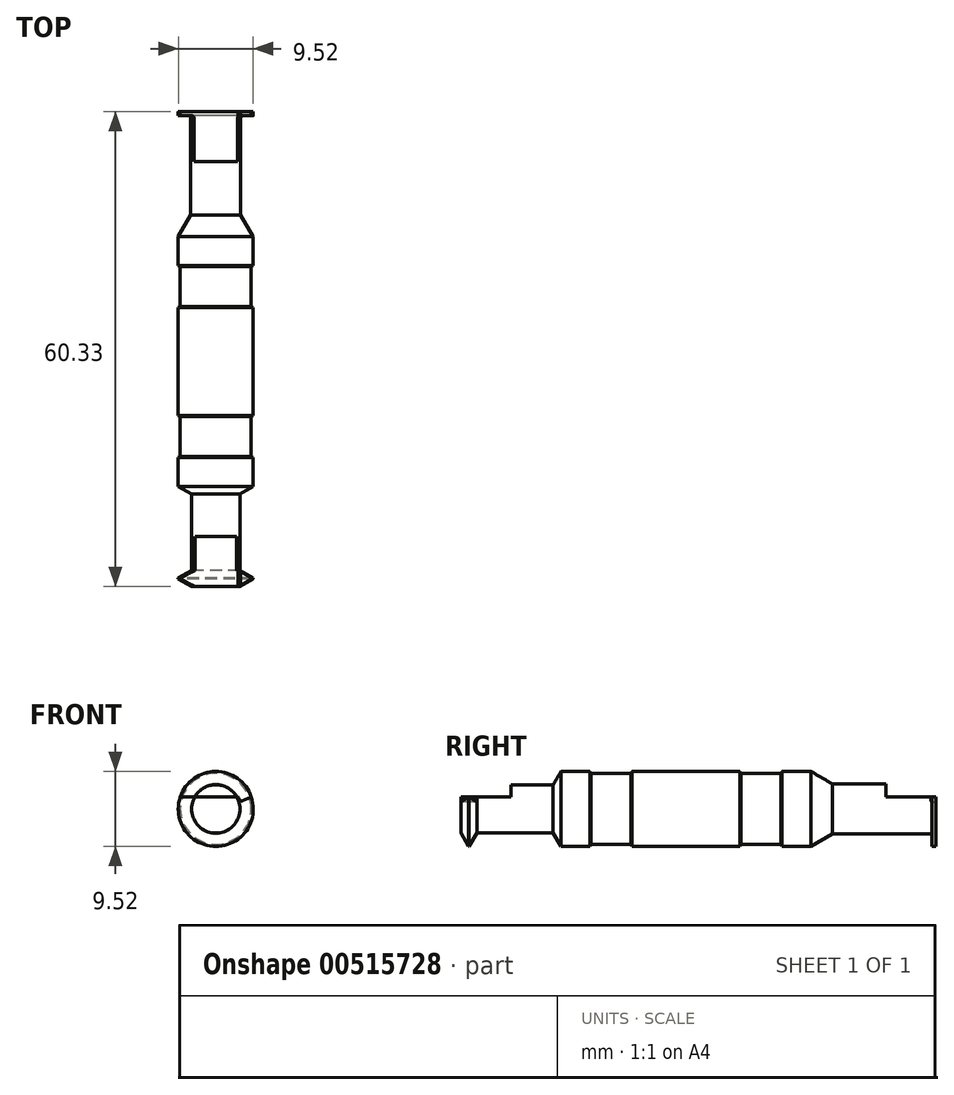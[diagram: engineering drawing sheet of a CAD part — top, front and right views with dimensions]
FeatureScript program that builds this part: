
annotation { "Feature Type Name" : "Feature", "Feature Type Description" : "" }
export const myFeature = defineFeature(function(context is Context, id is Id, definition is map)
    precondition{}
    {
        {
            var Q0;
            Q0=qCreatedBy(makeId("Top.planeOp"),FACE);
            cPlane(context, id + "F0", {"entities" : qUnion([Q0]), "cplaneType" : CPlaneType.OFFSET, "offset" : 1.52 * mm, "width" : 152.4 * mm, "height" : 152.4 * mm});
        }
        {
            var Q0;
            Q0=qCreatedBy(makeId("Right.planeOp"),FACE);
            var sketch = newSketch(context, id + "F1", { "sketchPlane" : qUnion([Q0])});
            skLineSegment(sketch, "E0", {"start": v(0, 4.76) * mm, "end": v(3.66, 4.76) * mm});
            skLineSegment(sketch, "E1", {"start": v(47.62, 4.76) * mm, "end": v(47.62, 0) * mm});
            skLineSegment(sketch, "E2", {"start": v(47.62, 0) * mm, "end": v(-12.7, 0) * mm});
            skLineSegment(sketch, "E3", {"start": v(-12.7, 0) * mm, "end": v(-12.7, 3.07) * mm});
            skLineSegment(sketch, "E4", {"start": v(-12.7, 3.07) * mm, "end": v(-11.72, 4.76) * mm});
            skLineSegment(sketch, "E5", {"start": v(-11.65, 4.76) * mm, "end": v(-10.67, 3.07) * mm});
            skLineSegment(sketch, "E6", {"start": v(-10.67, 3.07) * mm, "end": v(-0.98, 3.07) * mm});
            skLineSegment(sketch, "E7", {"start": v(-0.98, 3.07) * mm, "end": v(0, 4.76) * mm});
            skLineSegment(sketch, "E8", {"start": v(-11.72, 4.76) * mm, "end": v(-11.65, 4.76) * mm});
            skLineSegment(sketch, "E9", {"start": v(47.12, 4.76) * mm, "end": v(47.12, 3.43) * mm});
            skLineSegment(sketch, "E10", {"start": v(46.86, 3.18) * mm, "end": v(34.5, 3.18) * mm});
            skLineSegment(sketch, "E11", {"start": v(34.5, 3.18) * mm, "end": v(31.75, 4.76) * mm});
            skLineSegment(sketch, "E12.trimOffspring", {"start": v(47.12, 4.76) * mm, "end": v(47.62, 4.76) * mm});
            skPoint(sketch, "E13.visualSharp", {"position": v(47.12, 3.18) * mm});
            skArc(sketch, "E13.filletArc", {"start": v(46.86, 3.18) * mm, "mid": v(47.04, 3.25) * mm, "end": v(47.12, 3.43) * mm});
            skLineSegment(sketch, "E14", {"start": v(-11.72, 4.76) * mm, "end": v(-11.68, 4.83) * mm, "construction": true});
            skLineSegment(sketch, "E15", {"start": v(-11.68, 4.83) * mm, "end": v(-11.65, 4.76) * mm, "construction": true});
            skLineSegment(sketch, "E16", {"start": v(3.66, 4.76) * mm, "end": v(3.8, 4.5) * mm});
            skLineSegment(sketch, "E17", {"start": v(3.8, 4.5) * mm, "end": v(8.89, 4.5) * mm});
            skLineSegment(sketch, "E18", {"start": v(8.89, 4.5) * mm, "end": v(9.04, 4.76) * mm});
            skLineSegment(sketch, "E19.trimOffspring", {"start": v(9.04, 4.76) * mm, "end": v(22.71, 4.76) * mm});
            skLineSegment(sketch, "E20", {"start": v(6.35, 4.5) * mm, "end": v(6.35, 0) * mm, "construction": true});
            skLineSegment(sketch, "E21", {"start": v(22.71, 4.76) * mm, "end": v(22.86, 4.5) * mm});
            skLineSegment(sketch, "E22", {"start": v(22.86, 4.5) * mm, "end": v(27.94, 4.5) * mm});
            skLineSegment(sketch, "E23", {"start": v(27.94, 4.5) * mm, "end": v(28.09, 4.76) * mm});
            skLineSegment(sketch, "E24.trimOffspring", {"start": v(28.09, 4.76) * mm, "end": v(31.75, 4.76) * mm});
            skLineSegment(sketch, "E25", {"start": v(25.4, 4.5) * mm, "end": v(25.4, 0) * mm, "construction": true});
            skLineSegment(sketch, "E26", {"start": v(0, 0) * mm, "end": v(-33.3, 0) * mm, "construction": true});
            skSolve(sketch);
        }
        {
            var Q0;
            Q0 = qSketchRegion(id + "F1", true);
            var Q1;
            Q1=sQuery(id+"F1.wireOp",EDGE,"E2");
            revolve(context, id + "F2", {"entities" : qUnion([Q0]), "axis" : qUnion([Q1]), "revolveType" : RevolveType.FULL});
        }
        {
            var Q0;
            Q0=qCreatedBy(id+"F0.planeOp",FACE);
            var sketch = newSketch(context, id + "F3", { "sketchPlane" : qUnion([Q0])});
            skLineSegment(sketch, "E27.bottom", {"start": v(-6.35, -12.7) * mm, "end": v(6.35, -12.7) * mm});
            skLineSegment(sketch, "E27.top", {"start": v(-6.35, -6.35) * mm, "end": v(6.35, -6.35) * mm});
            skLineSegment(sketch, "E27.left", {"start": v(-6.35, -12.7) * mm, "end": v(-6.35, -6.35) * mm});
            skLineSegment(sketch, "E27.right", {"start": v(6.35, -12.7) * mm, "end": v(6.35, -6.35) * mm});
            skLineSegment(sketch, "E28", {"start": v(0, -6.35) * mm, "end": v(0, 0) * mm, "construction": true});
            skLineSegment(sketch, "E29.bottom", {"start": v(-6.35, 41.27) * mm, "end": v(6.35, 41.27) * mm});
            skLineSegment(sketch, "E29.top", {"start": v(-6.35, 47.62) * mm, "end": v(6.35, 47.62) * mm});
            skLineSegment(sketch, "E29.left", {"start": v(-6.35, 41.27) * mm, "end": v(-6.35, 47.62) * mm});
            skLineSegment(sketch, "E29.right", {"start": v(6.35, 41.27) * mm, "end": v(6.35, 47.62) * mm});
            skLineSegment(sketch, "E30", {"start": v(0, 41.27) * mm, "end": v(0, 0) * mm, "construction": true});
            skSolve(sketch);
        }
        {
            var Q0;
            Q0 = qSketchRegion(id + "F3", true);
            extrude(context, id + "F4", {"entities" : qUnion([Q0]), "operationType" : NewBodyOperationType.REMOVE, "endBound" : BoundingType.THROUGH_ALL, "depth" : 25.4 * mm, "offsetDistance" : 25.4 * mm});
        }
        {
            var Q0;
            Q0=makeQuery(id+"F2.opRevolve","SWEPT_FACE",FACE,{"disambiguationData":[OSD([sQuery(id+"F1.wireOp",EDGE,"E3")])]});
            var sketch = newSketch(context, id + "F5", { "sketchPlane" : qUnion([Q0])});
            skLineSegment(sketch, "E31", {"start": v(0, 0) * mm, "end": v(4.51, 1.52) * mm, "construction": true});
            skLineSegment(sketch, "E32", {"start": v(4.51, 1.52) * mm, "end": v(3.12, 0.91) * mm});
            skLineSegment(sketch, "E33", {"start": v(3.12, 0.91) * mm, "end": v(2.85, 1.52) * mm});
            skLineSegment(sketch, "E34", {"start": v(2.85, 1.52) * mm, "end": v(4.51, 1.52) * mm});
            skLineSegment(sketch, "E35", {"start": v(0, 0) * mm, "end": v(-9.1, -3.07) * mm, "construction": true});
            skCircle(sketch, "E36", {"center": v(-3.8, -1.28) * mm, "radius": 8.76 * mm, "construction": true});
            skCircle(sketch, "E37", {"center": v(-4.51, -1.52) * mm, "radius": 9.53 * mm, "construction": true});
            skCircle(sketch, "E38", {"center": v(-4.51, -1.52) * mm, "radius": 8.76 * mm, "construction": true});
            skSolve(sketch);
        }
        {
            var Q0;
            Q0 = qSketchRegion(id + "F5", true);
            extrude(context, id + "F6", {"entities" : qUnion([Q0]), "operationType" : NewBodyOperationType.REMOVE, "oppositeDirection" : true, "depth" : 2.3 * mm, "offsetDistance" : 25.4 * mm});
        }
        {
            var Q0;
            Q0=makeQuery(id+"F2.opRevolve","SWEPT_FACE",FACE,{"disambiguationData":[OSD([sQuery(id+"F1.wireOp",EDGE,"E1")])]});
            var sketch = newSketch(context, id + "F7", { "sketchPlane" : qUnion([Q0])});
            skLineSegment(sketch, "E39", {"start": v(-4.51, 1.52) * mm, "end": v(-3.12, 0.91) * mm});
            skLineSegment(sketch, "E40", {"start": v(-3.12, 0.91) * mm, "end": v(-2.85, 1.52) * mm});
            skLineSegment(sketch, "E41", {"start": v(-2.85, 1.52) * mm, "end": v(-4.51, 1.52) * mm});
            skSolve(sketch);
        }
        {
            var Q0;
            Q0 = qSketchRegion(id + "F7", true);
            extrude(context, id + "F8", {"entities" : qUnion([Q0]), "operationType" : NewBodyOperationType.REMOVE, "oppositeDirection" : true, "depth" : 1.27 * mm, "offsetDistance" : 25.4 * mm});
        }
    });
